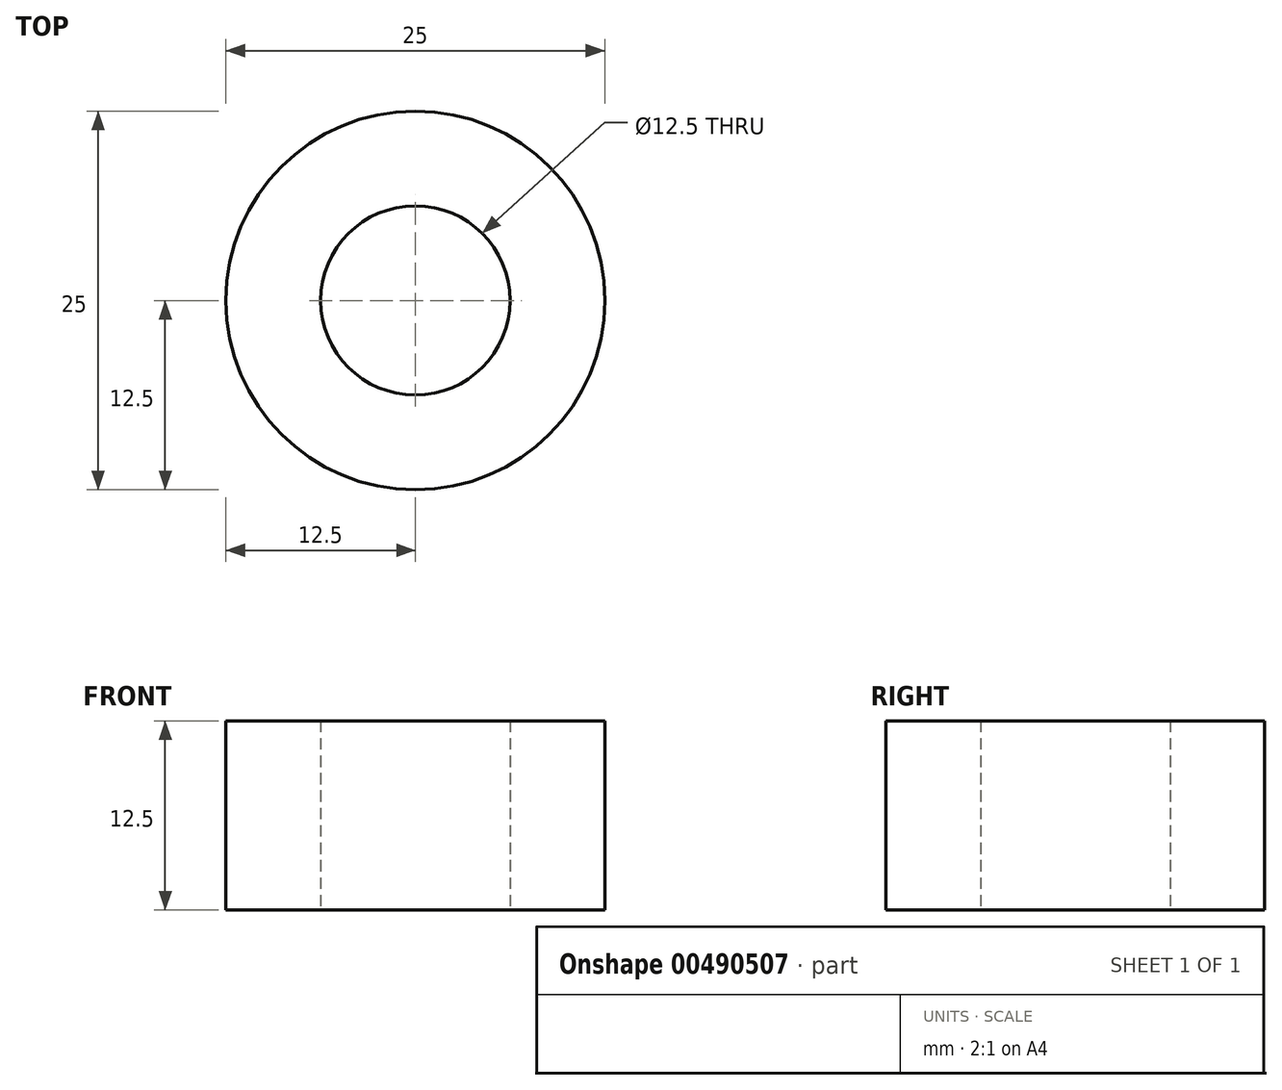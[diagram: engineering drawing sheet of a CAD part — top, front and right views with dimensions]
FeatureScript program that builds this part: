
annotation { "Feature Type Name" : "Feature", "Feature Type Description" : "" }
export const myFeature = defineFeature(function(context is Context, id is Id, definition is map)
    precondition{}
    {
        {
            var Q0;
            Q0=qCreatedBy(makeId("Top.planeOp"),FACE);
            var sketch = newSketch(context, id + "F0", { "sketchPlane" : qUnion([Q0])});
            skCircle(sketch, "E0", {"center": v(0, 0) * mm, "radius": 6.25 * mm});
            skCircle(sketch, "E1", {"center": v(0, 0) * mm, "radius": 12.5 * mm});
            skSolve(sketch);
        }
        {
            var Q0;
            Q0=makeQuery(id+"F0.imprint","IMPRINT",FACE,{"disambiguationData":[TD([[makeQuery(id+"F0.imprint","IMPRINT",EDGE,{"derivedFrom":sQuery(id+"F0.wireOp",EDGE,"E0")}),-1.0]])]});
            extrude(context, id + "F1", {"entities" : qUnion([Q0]), "depth" : 12.5 * mm});
        }
    });
